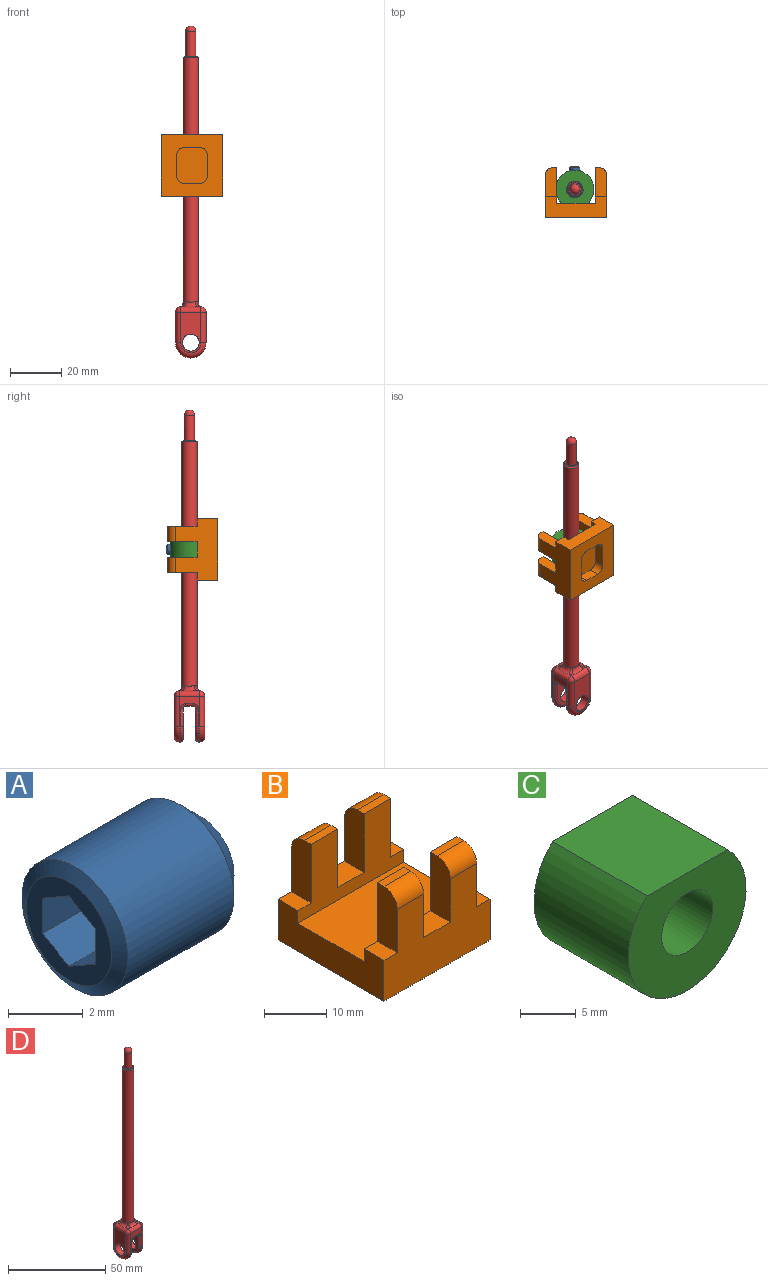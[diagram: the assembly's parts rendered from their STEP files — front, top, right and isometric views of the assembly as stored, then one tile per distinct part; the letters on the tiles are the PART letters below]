
ASSEMBLY  parts=4 mates=3
PART A: 12 faces, bbox 5x4x4 mm
  f0: plane 3.22x3.22mm, normal (-1,0,0), area 4.7mm2, adj f4,f5,f6,f7,f8,f9,f10
  f1: plane 2.5x2.5mm, normal (1,0,0), area 4.9mm2, adj f2
  f2: cone r=2mm half-angle=45deg, axis (-1,0,0), area 10.8mm2, adj f1,f3
  f3: cylinder r=2mm len=4.03mm, axis (-1,0,0), area 50.6mm2, adj f2,f4
  f4: cone r=1.61mm half-angle=60deg, axis (1,0,0), area 5.1mm2, adj f0,f3
  f5: plane 2.3x1mm, normal (0,-0.5,-0.87), area 2.7mm2, adj f0,f6,f10,f11
  f6: plane 2.3x1mm, normal (0,0.5,-0.87), area 2.7mm2, adj f0,f5,f7,f11
  f7: plane 2.3x1.15mm, normal (0,1,0), area 2.7mm2, adj f0,f6,f8,f11
  f8: plane 2.3x1mm, normal (0,0.5,0.87), area 2.7mm2, adj f0,f7,f9,f11
  f9: plane 2.3x1mm, normal (0,-0.5,0.87), area 2.7mm2, adj f0,f8,f10,f11
  f10: plane 2.3x1.15mm, normal (0,-1,0), area 2.7mm2, adj f0,f5,f9,f11
  f11: plane 2.31x2mm, normal (-1,0,0), area 3.5mm2, adj f5,f6,f7,f8,f9,f10
PART B: 39 faces, bbox 24x24x19.5 mm
  f0: plane 8x4mm, normal (0,-1,0), area 32mm2, adj f1,f11,f12,f14
  f1: cylinder r=3mm len=4mm, axis (0,0,1), area 18.8mm2, adj f0,f2,f12,f14
  f2: plane 6x4mm, normal (-1,0,0), area 24mm2, adj f1,f3,f12,f14
  f3: cylinder r=3mm len=4mm, axis (0,0,1), area 18.8mm2, adj f2,f4,f12,f14
  f4: plane 8x4mm, normal (0,1,0), area 32mm2, adj f3,f5,f12,f14
  f5: cylinder r=3mm len=4mm, axis (0,0,1), area 18.8mm2, adj f4,f6,f12,f14
  f6: plane 6x4mm, normal (1,0,0), area 24mm2, adj f5,f11,f12,f14
  f7: plane 24x8mm, normal (-1,0,0), area 154.5mm2, adj f8,f10,f12,f13,f15,f18,f19,f22
  f8: plane 24x16.5mm, normal (0,-1,0), area 294mm2, adj f7,f9,f12,f20,f21,f22,f29,f30
  f9: plane 24x8mm, normal (1,0,0), area 154.5mm2, adj f8,f10,f12,f13,f15,f16,f19,f20
  f10: plane 24x16.5mm, normal (0,1,0), area 294mm2, adj f7,f9,f12,f16,f17,f18,f23,f24
  f11: cylinder r=3mm len=4mm, axis (0,0,1), area 18.8mm2, adj f0,f6,f12,f14
  f12: plane 24x24mm, normal (0,0,-1), area 415.7mm2, adj f0,f1,f2,f3,f4,f5,f6,f7
  f13: plane 24x15mm, normal (0,0,1), area 360mm2, adj f7,f9,f15,f19
  f14: plane 14x12mm, normal (0,0,-1), area 160.3mm2, adj f0,f1,f2,f3,f4,f5,f6,f11
  f15: plane 24x14mm, normal (0,-1,0), area 198mm2, adj f7,f9,f13,f16,f17,f18,f23,f24
  f16: plane 4.5x3mm, normal (0,0,1), area 13.5mm2, adj f9,f10,f15,f24
  f17: plane 6x4.5mm, normal (0,0,1), area 27mm2, adj f10,f15,f23,f27
  f18: plane 4.5x3mm, normal (0,0,1), area 13.5mm2, adj f7,f10,f15,f26
  f19: plane 24x14mm, normal (0,1,0), area 198mm2, adj f7,f9,f13,f20,f21,f22,f29,f30
  f20: plane 4.5x3mm, normal (0,0,1), area 13.5mm2, adj f8,f9,f19,f29
  f21: plane 6x4.5mm, normal (0,0,1), area 27mm2, adj f8,f19,f30,f33
  f22: plane 4.5x3mm, normal (0,0,1), area 13.5mm2, adj f7,f8,f19,f32
  f23: plane 11.5x4.5mm, normal (-1,0,0), area 49.8mm2, adj f10,f15,f17,f25,f37
  f24: plane 11.5x4.5mm, normal (1,0,0), area 49.8mm2, adj f10,f15,f16,f25,f37
  f25: plane 6x1.5mm, normal (0,0,1), area 9mm2, adj f15,f23,f24,f37
  f26: plane 11.5x4.5mm, normal (-1,0,0), area 49.8mm2, adj f10,f15,f18,f28,f38
  f27: plane 11.5x4.5mm, normal (1,0,0), area 49.8mm2, adj f10,f15,f17,f28,f38
  f28: plane 6x1.5mm, normal (0,0,1), area 9mm2, adj f15,f26,f27,f38
  f29: plane 11.5x4.5mm, normal (1,0,0), area 49.8mm2, adj f8,f19,f20,f31,f36
  f30: plane 11.5x4.5mm, normal (-1,0,0), area 49.8mm2, adj f8,f19,f21,f31,f36
  f31: plane 6x1.5mm, normal (0,0,1), area 9mm2, adj f19,f29,f30,f36
  f32: plane 11.5x4.5mm, normal (-1,0,0), area 49.8mm2, adj f8,f19,f22,f34,f35
  f33: plane 11.5x4.5mm, normal (1,0,0), area 49.8mm2, adj f8,f19,f21,f34,f35
  f34: plane 6x1.5mm, normal (0,0,1), area 9mm2, adj f19,f32,f33,f35
  f35: cylinder r=3mm len=6mm, axis (1,0,0), area 28.3mm2, adj f8,f32,f33,f34
  f36: cylinder r=3mm len=6mm, axis (1,0,0), area 28.3mm2, adj f8,f29,f30,f31
  f37: cylinder r=3mm len=6mm, axis (-1,0,0), area 28.3mm2, adj f10,f23,f24,f25
  f38: cylinder r=3mm len=6mm, axis (-1,0,0), area 28.3mm2, adj f10,f26,f27,f28
PART C: 6 faces, bbox 15x12x13 mm
  f0: cylinder r=2.1mm len=5.02mm, axis (0,0,-1), area 59.2mm2, adj f1,f2
  f1: cylinder r=3.25mm len=12mm, axis (0,-1,0), area 235.5mm2, adj f0,f3,f4
  f2: cylinder r=7.5mm len=15mm, axis (0,-1,0), area 422mm2, adj f0,f3,f4,f5
  f3: plane 15x13mm, normal (0,1,0), area 129.5mm2, adj f1,f2,f5
  f4: plane 15x13mm, normal (0,-1,0), area 129.5mm2, adj f1,f2,f5
  f5: plane 12x10.2mm, normal (0,0,1), area 122.4mm2, adj f2,f3,f4
PART D: 56 faces, bbox 12x13x130.5 mm
  f0: plane 1x1mm, normal (0,0,1), area 0.5mm2, adj f27,f28,f37
  f1: plane 1x1mm, normal (0,0,1), area 0.5mm2, adj f21,f27,f33
  f2: plane 1x1mm, normal (0,0,1), area 0.5mm2, adj f21,f22,f34
  f3: cylinder r=3mm len=95.63mm, axis (0,0,-1), area 1801.2mm2, adj f32,f33,f34,f35,f36,f37,f38,f39
  f4: plane 5x5mm, normal (0,0,1), area 7.1mm2, adj f5,f55
  f5: cylinder r=2mm len=10mm, axis (0,0,-1), area 125.7mm2, adj f4,f54
  f6: plane 1x1mm, normal (0,0,1), area 0.5mm2, adj f22,f28,f38
  f7: plane 12x8mm, normal (0,1,0), area 34.7mm2, adj f16,f17,f18,f21,f26,f48,f49,f51
  f8: plane 12x8mm, normal (0,-1,0), area 34.7mm2, adj f16,f17,f23,f28,f31,f40,f41,f42
  f9: plane 10x3mm, normal (0,0,-1), area 30mm2, adj f42,f47,f50,f53
  f10: plane 12x10mm, normal (-1,0,0), area 75.1mm2, adj f15,f40,f44,f47,f48
  f11: plane 16x8mm, normal (1,0,0), area 86.9mm2, adj f15,f18,f20,f22,f23
  f12: plane 12x10mm, normal (1,0,0), area 75.1mm2, adj f14,f41,f45,f49,f50
  f13: plane 16x8mm, normal (-1,0,0), area 86.9mm2, adj f14,f26,f27,f29,f31
  f14: cylinder r=3.3mm len=6.6mm, axis (-1,0,0), area 72.6mm2, adj f12,f13
  f15: cylinder r=3.3mm len=6.6mm, axis (-1,0,0), area 72.6mm2, adj f10,f11
  f16: cylinder r=6mm len=12mm, axis (1,0,0), area 9.4mm2, adj f7,f8,f20,f44
  f17: cylinder r=6mm len=12mm, axis (-1,0,0), area 9.4mm2, adj f7,f8,f29,f45
  f18: cylinder r=2mm len=12mm, axis (0,0,1), area 37.7mm2, adj f7,f11,f19,f20
  f19: sphere r=2mm, area 6.3mm2, adj f18,f21,f22
  f20: torus R=4mm, axis (1,0,0), area 52mm2, adj f11,f16,f18,f23
  f21: cylinder r=2mm len=8mm, axis (-1,0,0), area 23.1mm2, adj f1,f2,f7,f19,f24,f32
  f22: cylinder r=2mm len=8mm, axis (0,1,0), area 23.1mm2, adj f2,f6,f11,f19,f25,f36
  f23: cylinder r=2mm len=12mm, axis (0,0,-1), area 37.7mm2, adj f8,f11,f20,f25
  f24: sphere r=2mm, area 6.3mm2, adj f21,f26,f27
  f25: sphere r=2mm, area 6.3mm2, adj f22,f23,f28
  f26: cylinder r=2mm len=12mm, axis (0,0,-1), area 37.7mm2, adj f7,f13,f24,f29
  f27: cylinder r=2mm len=8mm, axis (0,-1,0), area 23.1mm2, adj f0,f1,f13,f24,f30,f35
  f28: cylinder r=2mm len=8mm, axis (1,0,0), area 23.1mm2, adj f0,f6,f8,f25,f30,f39
  f29: torus R=4mm, axis (1,0,0), area 52mm2, adj f13,f17,f26,f31
  f30: sphere r=2mm, area 6.3mm2, adj f27,f28,f31
  f31: cylinder r=2mm len=12mm, axis (0,0,1), area 37.7mm2, adj f8,f13,f29,f30
  f32: bspline ~7.31x2.45mm, area 13mm2, adj f3,f21,f33,f34
  f33: torus R=5mm, axis (0,0,1), area 3.3mm2, adj f1,f3,f32,f35
  f34: torus R=5mm, axis (0,0,1), area 3.3mm2, adj f2,f3,f32,f36
  f35: bspline ~7.31x2.45mm, area 13mm2, adj f3,f27,f33,f37
  f36: bspline ~7.31x2.45mm, area 13mm2, adj f3,f22,f34,f38
  f37: torus R=5mm, axis (0,0,1), area 3.3mm2, adj f0,f3,f35,f39
  f38: torus R=5mm, axis (0,0,1), area 3.3mm2, adj f3,f6,f36,f39
  f39: bspline ~7.31x2.45mm, area 13mm2, adj f3,f28,f37,f38
  f40: cylinder r=1mm len=7mm, axis (0,0,-1), area 11mm2, adj f8,f10,f43,f44
  f41: cylinder r=1mm len=7mm, axis (0,0,1), area 11mm2, adj f8,f12,f45,f46
  f42: cylinder r=1mm len=3mm, axis (-1,0,0), area 4.7mm2, adj f8,f9,f43,f46
  f43: torus R=2mm, axis (0,1,0), area 3.4mm2, adj f8,f40,f42,f47
  f44: torus R=5mm, axis (-1,0,0), area 27.8mm2, adj f10,f16,f40,f48
  f45: torus R=5mm, axis (-1,0,0), area 27.8mm2, adj f12,f17,f41,f49
  f46: torus R=2mm, axis (0,1,0), area 3.4mm2, adj f8,f41,f42,f50
  f47: cylinder r=1mm len=10mm, axis (0,-1,0), area 15.7mm2, adj f9,f10,f43,f51
  f48: cylinder r=1mm len=7mm, axis (0,0,1), area 11mm2, adj f7,f10,f44,f51
  f49: cylinder r=1mm len=7mm, axis (0,0,-1), area 11mm2, adj f7,f12,f45,f52
  f50: cylinder r=1mm len=10mm, axis (0,1,0), area 15.7mm2, adj f9,f12,f46,f52
  f51: torus R=2mm, axis (0,1,0), area 3.4mm2, adj f7,f47,f48,f53
  f52: torus R=2mm, axis (0,1,0), area 3.4mm2, adj f7,f49,f50,f53
  f53: cylinder r=1mm len=3mm, axis (1,0,0), area 4.7mm2, adj f7,f9,f51,f52
  f54: sphere r=2mm, area 25.1mm2, adj f5
  f55: cone r=2.5mm half-angle=45deg, axis (0,0,-1), area 12.2mm2, adj f3,f4
PLACE A rot(axis=(0,0,-1),90deg) t=(-0.48,8.54,55.4)mm
PLACE B rot(axis=(-0.58,0.58,0.58),120deg) t=(0,-7.43,55.4)mm
PLACE C rot(axis=(1,0,0),90deg) t=(-0.48,-0.43,49.4)mm
PLACE D rot(axis=(0,0,1),90deg) t=(-0.48,-0.43,0)mm
MATE cylindrical C.f1 <-> D.f3  axis (0,0,-1) through (-0.48,-0.43,49.4)mm
MATE planar C.f0 <-> B.f13  axis (0,-1,0) through (-0.48,-5.93,55.4)mm
MATE cylindrical C.f0 <-> A.f3  axis (0,1,0) through (-0.48,4.56,55.4)mm
